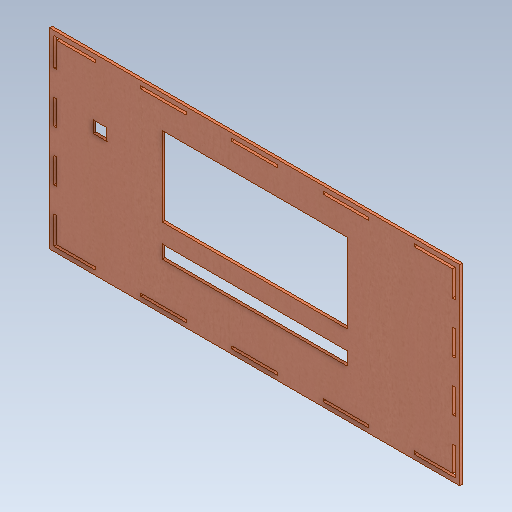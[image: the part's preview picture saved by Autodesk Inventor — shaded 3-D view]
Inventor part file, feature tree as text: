
AUTODESK INVENTOR PART (.ipt)
format: ipt  version: 2020.3 (Build 243373000, 373)  size: 314,368 bytes
history: native  units: mm
features: other x1, extrude x1
ambient origin geometry x8: Origin, YZ Plane, XZ Plane, XY Plane, X Axis, Y Axis, Z Axis, Center Point
bodies: Body1 (feature_tree)
feature tree (2):
  other  "Sólido1"
  extrude  "Extrusión1"  Depth=210.0mm
